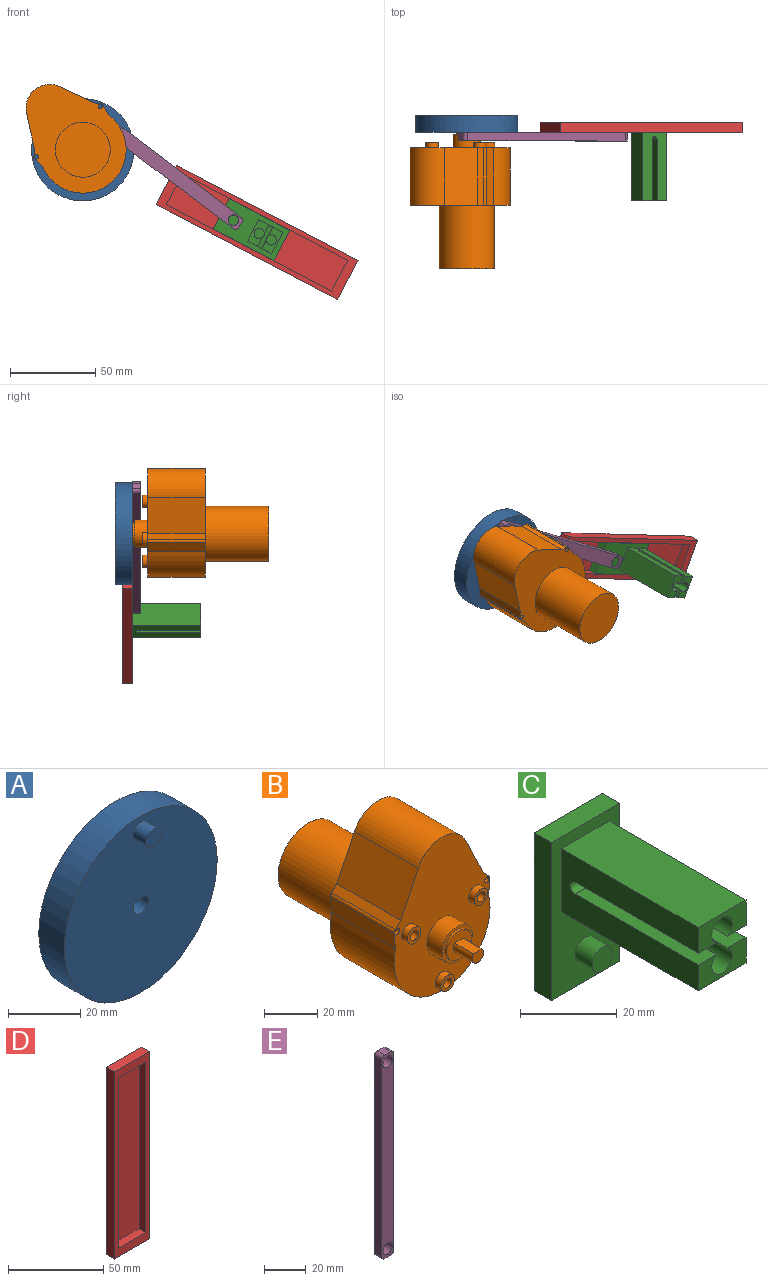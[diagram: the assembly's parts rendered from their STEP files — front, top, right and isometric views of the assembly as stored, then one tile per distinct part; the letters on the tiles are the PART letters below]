
ASSEMBLY  parts=5 mates=4
PART A: 7 faces, bbox 60x15x60 mm
  f0: cylinder r=3mm len=6mm, axis (0,1,0), area 94.2mm2, adj f1,f5
  f1: plane 6x6mm, normal (0,-1,0), area 28.3mm2, adj f0
  f2: cylinder r=3mm len=10mm, axis (0,1,0), area 138mm2, adj f3,f5,f6
  f3: plane 10x4.47mm, normal (0,0,-1), area 44.7mm2, adj f2,f5,f6
  f4: cylinder r=30mm len=60mm, axis (0,1,0), area 1885mm2, adj f5,f6
  f5: plane 60x60mm, normal (0,-1,0), area 2774mm2, adj f0,f2,f3,f4
  f6: plane 60x60mm, normal (0,1,0), area 2802.3mm2, adj f2,f3,f4
PART B: 35 faces, bbox 50.9x89.9x70.5 mm
  f0: plane 13x13mm, normal (0,-1,0), area 107.6mm2, adj f3,f4,f5
  f1: cylinder r=8mm len=16mm, axis (0,1,0), area 402.1mm2, adj f2,f20
  f2: plane 16x16mm, normal (0,-1,0), area 68.3mm2, adj f1,f3
  f3: cylinder r=6.5mm len=13mm, axis (0,1,0), area 40.8mm2, adj f0,f2
  f4: plane 10x4.47mm, normal (0,0,1), area 44.7mm2, adj f0,f5,f6
  f5: cylinder r=3mm len=10mm, axis (0,1,0), area 138mm2, adj f0,f4,f6
  f6: plane 6x5mm, normal (0,-1,0), area 25.2mm2, adj f4,f5
  f7: plane 33.8x19.35mm, normal (0.9,0,0.44), area 726.8mm2, adj f8,f18,f19,f20
  f8: cylinder r=14mm len=33.8mm, axis (0,-1,0), area 1059.4mm2, adj f7,f9,f19,f20
  f9: plane 33.8x19.35mm, normal (-0.9,0,0.44), area 726.8mm2, adj f8,f10,f19,f20
  f10: plane 33.8x2.9mm, normal (-0.74,0,0.68), area 133.1mm2, adj f9,f11,f19,f20
  f11: cylinder r=1.6mm len=33.8mm, axis (0,-1,0), area 55.9mm2, adj f10,f12,f19,f20
  f12: plane 33.8x7.37mm, normal (-1,0,-0.09), area 250.1mm2, adj f11,f13,f19,f20
  f13: cylinder r=25.45mm len=50.9mm, axis (0,-1,0), area 3119.2mm2, adj f12,f14,f19,f20
  f14: plane 33.8x7.37mm, normal (1,0,-0.09), area 250.1mm2, adj f13,f15,f19,f20
  f15: cylinder r=1.6mm len=33.8mm, axis (0,-1,0), area 55.9mm2, adj f14,f18,f19,f20
  f16: cylinder r=1.25mm len=33.8mm, axis (0,-1,0), area 265.5mm2, adj f19,f20
  f17: cylinder r=1.25mm len=33.8mm, axis (0,-1,0), area 265.5mm2, adj f19,f20
  f18: plane 33.8x2.9mm, normal (0.74,0,0.68), area 133.1mm2, adj f7,f15,f19,f20
  f19: plane 70.45x50.9mm, normal (0,1,0), area 1886.6mm2, adj f7,f8,f9,f10,f11,f12,f13,f14
  f20: plane 70.45x50.9mm, normal (0,-1,0), area 2377.7mm2, adj f1,f7,f8,f9,f10,f11,f12,f13
  f21: cylinder r=2.1mm len=9mm, axis (0,1,0), area 118.8mm2, adj f23,f32
  f22: cylinder r=3.6mm len=7.2mm, axis (0,1,0), area 67.9mm2, adj f20,f23
  f23: plane 7.2x7.2mm, normal (0,-1,0), area 26.9mm2, adj f21,f22
  f24: cylinder r=2.1mm len=9mm, axis (0,1,0), area 118.8mm2, adj f26,f31
  f25: cylinder r=3.6mm len=7.2mm, axis (0,1,0), area 67.9mm2, adj f20,f26
  f26: plane 7.2x7.2mm, normal (0,-1,0), area 26.9mm2, adj f24,f25
  f27: cylinder r=2.1mm len=9mm, axis (0,1,0), area 118.8mm2, adj f29,f30
  f28: cylinder r=3.6mm len=7.2mm, axis (0,1,0), area 67.9mm2, adj f20,f29
  f29: plane 7.2x7.2mm, normal (0,-1,0), area 26.9mm2, adj f27,f28
  f30: plane 4.2x4.2mm, normal (0,-1,0), area 13.9mm2, adj f27
  f31: plane 4.2x4.2mm, normal (0,-1,0), area 13.9mm2, adj f24
  f32: plane 4.2x4.2mm, normal (0,-1,0), area 13.9mm2, adj f21
  f33: cylinder r=16.1mm len=37.1mm, axis (0,-1,0), area 3753mm2, adj f19,f34
  f34: plane 32.2x32.2mm, normal (0,1,0), area 814.3mm2, adj f33
PART C: 23 faces, bbox 20x45x40 mm
  f0: plane 36x5.34mm, normal (0,0,-1), area 192.3mm2, adj f2,f4,f18,f19
  f1: plane 36x5.34mm, normal (0,0,1), area 192.3mm2, adj f4,f13,f18,f21
  f2: plane 14x6.5mm, normal (0,-1,0), area 63.9mm2, adj f0,f3,f4,f11,f14,f19
  f3: plane 40x16mm, normal (-1,0,0), area 528.5mm2, adj f2,f5,f11,f12,f13,f14,f15,f18
  f4: plane 40x16mm, normal (1,0,0), area 528.5mm2, adj f0,f1,f2,f5,f11,f12,f13,f18
  f5: plane 40x20mm, normal (0,-1,0), area 547.7mm2, adj f3,f4,f6,f7,f8,f9,f11,f12
  f6: plane 20x5mm, normal (0,0,1), area 100mm2, adj f5,f7,f9,f10
  f7: plane 40x5mm, normal (-1,0,0), area 200mm2, adj f5,f6,f8,f10
  f8: plane 20x5mm, normal (0,0,-1), area 100mm2, adj f5,f7,f9,f10
  f9: plane 40x5mm, normal (1,0,0), area 200mm2, adj f5,f6,f8,f10
  f10: plane 40x20mm, normal (0,1,0), area 800mm2, adj f6,f7,f8,f9
  f11: plane 40x14mm, normal (0,0,1), area 560mm2, adj f2,f3,f4,f5
  f12: plane 40x14mm, normal (0,0,-1), area 560mm2, adj f3,f4,f5,f13
  f13: plane 14x6.5mm, normal (0,-1,0), area 63.9mm2, adj f1,f3,f4,f12,f15,f21
  f14: plane 36x5.34mm, normal (0,0,-1), area 192.3mm2, adj f2,f3,f18,f19
  f15: plane 36x5.34mm, normal (0,0,1), area 192.3mm2, adj f3,f13,f18,f21
  f16: cylinder r=3mm len=6mm, axis (0,1,0), area 94.2mm2, adj f5,f17
  f17: plane 6x6mm, normal (0,-1,0), area 28.3mm2, adj f16
  f18: cylinder r=1.5mm len=14mm, axis (-1,0,0), area 59.4mm2, adj f0,f1,f3,f4,f14,f15,f19,f21
  f19: cylinder r=3mm len=40mm, axis (0,-1,0), area 624.3mm2, adj f0,f2,f14,f18,f20
  f20: plane 6x6mm, normal (0,-1,0), area 28.3mm2, adj f19
  f21: cylinder r=3mm len=40mm, axis (0,-1,0), area 624.3mm2, adj f1,f13,f15,f18,f22
  f22: plane 6x6mm, normal (0,-1,0), area 28.3mm2, adj f21
PART D: 11 faces, bbox 26x6x120 mm
  f0: plane 26x6mm, normal (0,0,1), area 156mm2, adj f1,f7,f8,f9
  f1: plane 120x6mm, normal (-1,0,0), area 720mm2, adj f0,f2,f8,f9
  f2: plane 26x6mm, normal (0,0,-1), area 156mm2, adj f1,f7,f8,f9
  f3: plane 109.2x5mm, normal (1,0,0), area 546mm2, adj f4,f6,f8,f10
  f4: plane 20.4x5mm, normal (0,0,-1), area 102mm2, adj f3,f5,f8,f10
  f5: plane 109.2x5mm, normal (-1,0,0), area 546mm2, adj f4,f6,f8,f10
  f6: plane 20.4x5mm, normal (0,0,1), area 102mm2, adj f3,f5,f8,f10
  f7: plane 120x6mm, normal (1,0,0), area 720mm2, adj f0,f2,f8,f9
  f8: plane 120x26mm, normal (0,-1,0), area 892.3mm2, adj f0,f1,f2,f3,f4,f5,f6,f7
  f9: plane 120x26mm, normal (0,1,0), area 3120mm2, adj f0,f1,f2,f7
  f10: plane 109.2x20.4mm, normal (0,-1,0), area 2227.7mm2, adj f3,f4,f5,f6
PART E: 12 faces, bbox 8x5x120 mm
  f0: plane 5x4mm, normal (0,0,1), area 20mm2, adj f1,f9,f10,f11
  f1: cylinder r=2mm len=5mm, axis (0,1,0), area 15.7mm2, adj f0,f2,f10,f11
  f2: plane 116x5mm, normal (-1,0,0), area 580mm2, adj f1,f3,f10,f11
  f3: cylinder r=2mm len=5mm, axis (0,1,0), area 15.7mm2, adj f2,f4,f10,f11
  f4: plane 5x4mm, normal (0,0,-1), area 20mm2, adj f3,f5,f10,f11
  f5: cylinder r=2mm len=5mm, axis (0,1,0), area 15.7mm2, adj f4,f6,f10,f11
  f6: plane 116x5mm, normal (1,0,0), area 580mm2, adj f5,f9,f10,f11
  f7: cylinder r=3.2mm len=6.4mm, axis (0,1,0), area 100.5mm2, adj f10,f11
  f8: cylinder r=3.2mm len=6.4mm, axis (0,1,0), area 100.5mm2, adj f10,f11
  f9: cylinder r=2mm len=5mm, axis (0,1,0), area 15.7mm2, adj f0,f6,f10,f11
  f10: plane 120x8mm, normal (0,-1,0), area 892.2mm2, adj f0,f1,f2,f3,f4,f5,f6,f7
  f11: plane 120x8mm, normal (0,1,0), area 892.2mm2, adj f0,f1,f2,f3,f4,f5,f6,f7
PLACE A rot(axis=(0,1,0),0.9deg) t=(-1.99,2.77,65.45)mm
PLACE B rot(axis=(-0.33,0,0.94),180deg) t=(-1.99,-16.23,65.45)mm fixed
PLACE C rot(axis=(0,1,0),117.6deg) t=(96.99,-2.23,18.63)mm
PLACE D rot(axis=(0,1,0),117.6deg) t=(100.14,-1.23,16.98)mm fixed
PLACE E rot(axis=(0,-1,0),52.9deg) t=(42.47,-7.23,57.35)mm
MATE revolute C.f16 <-> E.f7  axis (0,1,0) through (86.36,-9.73,24.19)mm
MATE revolute B.f5 <-> A.f2  axis (0,-1,0) through (-1.99,-2.23,65.45)mm
MATE slider C.f8 <-> D.f4  axis (-0.89,0,0.46) through (79.27,-4.73,27.9)mm
MATE planar E.f8 <-> A.f0  axis (0,1,0) through (-1.41,-9.73,90.51)mm
